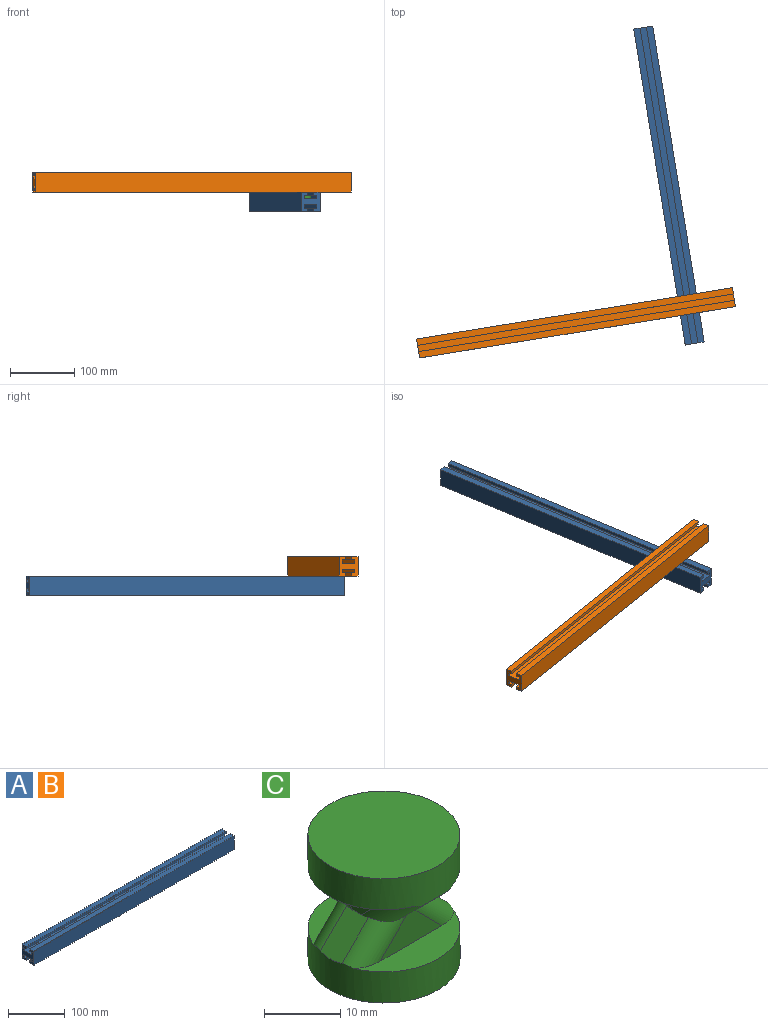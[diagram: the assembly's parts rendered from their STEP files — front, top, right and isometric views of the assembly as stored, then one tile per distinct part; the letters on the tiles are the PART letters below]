
ASSEMBLY  parts=3 mates=4
PART A: 22 faces, bbox 500x30x30 mm
  f0: plane 500x5mm, normal (0,-1,0), area 2500mm2, adj f1,f19,f20,f21
  f1: plane 500x20mm, normal (0,0,1), area 10000mm2, adj f0,f2,f20,f21
  f2: plane 500x5mm, normal (0,1,0), area 2500mm2, adj f1,f3,f20,f21
  f3: plane 500x5mm, normal (0,0,-1), area 2500mm2, adj f2,f4,f20,f21
  f4: plane 500x5mm, normal (0,1,0), area 2500mm2, adj f3,f5,f20,f21
  f5: plane 500x10mm, normal (0,0,1), area 5000mm2, adj f4,f6,f20,f21
  f6: plane 500x30mm, normal (0,-1,0), area 15000mm2, adj f5,f7,f20,f21
  f7: plane 500x10mm, normal (0,0,-1), area 5000mm2, adj f6,f8,f20,f21
  f8: plane 500x5mm, normal (0,1,0), area 2500mm2, adj f7,f9,f20,f21
  f9: plane 500x5mm, normal (0,0,1), area 2500mm2, adj f8,f10,f20,f21
  f10: plane 500x5mm, normal (0,1,0), area 2500mm2, adj f9,f11,f20,f21
  f11: plane 500x20mm, normal (0,0,-1), area 10000mm2, adj f10,f12,f20,f21
  f12: plane 500x5mm, normal (0,-1,0), area 2500mm2, adj f11,f13,f20,f21
  f13: plane 500x5mm, normal (0,0,1), area 2500mm2, adj f12,f14,f20,f21
  f14: plane 500x5mm, normal (0,-1,0), area 2500mm2, adj f13,f15,f20,f21
  f15: plane 500x10mm, normal (0,0,-1), area 5000mm2, adj f14,f16,f20,f21
  f16: plane 500x30mm, normal (0,1,0), area 15000mm2, adj f15,f17,f20,f21
  f17: plane 500x10mm, normal (0,0,1), area 5000mm2, adj f16,f18,f20,f21
  f18: plane 500x5mm, normal (0,-1,0), area 2500mm2, adj f17,f19,f20,f21
  f19: plane 500x5mm, normal (0,0,-1), area 2500mm2, adj f0,f18,f20,f21
  f20: plane 30x30mm, normal (1,0,0), area 600mm2, adj f0,f1,f2,f3,f4,f5,f6,f7
  f21: plane 30x30mm, normal (-1,0,0), area 600mm2, adj f0,f1,f2,f3,f4,f5,f6,f7
PART B: same geometry as A
PART C: 24 faces, bbox 20x20x20 mm
  f0: plane 11.51x5mm, normal (0,-1,0), area 32.6mm2, adj f1,f14,f18,f22
  f1: plane 18.63x6.37mm, normal (0,0,1), area 63.5mm2, adj f0,f7,f18,f22
  f2: plane 20x20mm, normal (0,0,-1), area 314.2mm2, adj f7
  f3: plane 18.63x6.37mm, normal (0,0,1), area 63.5mm2, adj f4,f7,f16,f20
  f4: plane 11.51x5mm, normal (0,1,0), area 32.6mm2, adj f3,f13,f16,f20
  f5: plane 5.11x5.11mm, normal (-0.71,0,0.71), area 28mm2, adj f7,f8,f16,f17,f18,f19
  f6: plane 5.11x5.11mm, normal (0.71,0,0.71), area 28mm2, adj f7,f12,f20,f21,f22,f23
  f7: cylinder r=10mm len=20mm, axis (0,0,1), area 316mm2, adj f1,f2,f3,f5,f6,f16,f18,f20
  f8: plane 11.51x5mm, normal (-1,0,0), area 32.6mm2, adj f5,f9,f17,f19
  f9: plane 18.63x6.37mm, normal (0,0,-1), area 63.5mm2, adj f8,f15,f17,f19
  f10: plane 20x20mm, normal (0,0,1), area 314.2mm2, adj f15
  f11: plane 18.63x6.37mm, normal (0,0,-1), area 63.5mm2, adj f12,f15,f21,f23
  f12: plane 11.51x5mm, normal (1,0,0), area 32.6mm2, adj f6,f11,f21,f23
  f13: plane 5.11x5.11mm, normal (0,0.71,-0.71), area 28mm2, adj f4,f15,f16,f17,f20,f21
  f14: plane 5.11x5.11mm, normal (0,-0.71,-0.71), area 28mm2, adj f0,f15,f18,f19,f22,f23
  f15: cylinder r=10mm len=20mm, axis (0,0,-1), area 316mm2, adj f9,f10,f11,f13,f14,f17,f19,f21
  f16: cylinder r=3mm len=9.04mm, axis (0.71,0,0.71), area 32.9mm2, adj f3,f4,f5,f7,f13,f17
  f17: cylinder r=3mm len=9.04mm, axis (0,-0.71,-0.71), area 32.9mm2, adj f5,f8,f9,f13,f15,f16
  f18: cylinder r=3mm len=9.04mm, axis (0.71,0,0.71), area 32.9mm2, adj f0,f1,f5,f7,f14,f19
  f19: cylinder r=3mm len=9.04mm, axis (0,0.71,-0.71), area 32.9mm2, adj f5,f8,f9,f14,f15,f18
  f20: cylinder r=3mm len=9.04mm, axis (-0.71,0,0.71), area 32.9mm2, adj f3,f4,f6,f7,f13,f21
  f21: cylinder r=3mm len=9.04mm, axis (0,-0.71,-0.71), area 32.9mm2, adj f6,f11,f12,f13,f15,f20
  f22: cylinder r=3mm len=9.04mm, axis (-0.71,0,0.71), area 32.9mm2, adj f0,f1,f6,f7,f14,f23
  f23: cylinder r=3mm len=9.04mm, axis (0,0.71,-0.71), area 32.9mm2, adj f6,f11,f12,f14,f15,f22
PLACE A rot(axis=(0,0,-1),80.8deg) t=(256.26,337.04,-59.76)mm
PLACE B rot(axis=(1,0.08,0),180deg) t=(111.02,122.48,-29.76)mm
PLACE C rot(axis=(-1,-0.08,0),180deg) t=(286.51,151.02,-29.76)mm
MATE planar C.f7 <-> B.f1  axis (0,0,1) through (286.51,151.02,-34.76)mm
MATE planar C.f7 <-> A.f1  axis (0,0,-1) through (286.51,151.02,-54.76)mm
MATE planar C.f12 <-> A.f18  axis (0.99,0.16,0) through (291.45,151.83,-47.9)mm
MATE planar C.f4 <-> B.f18  axis (0.16,-0.99,0) through (287.31,146.09,-41.62)mm
